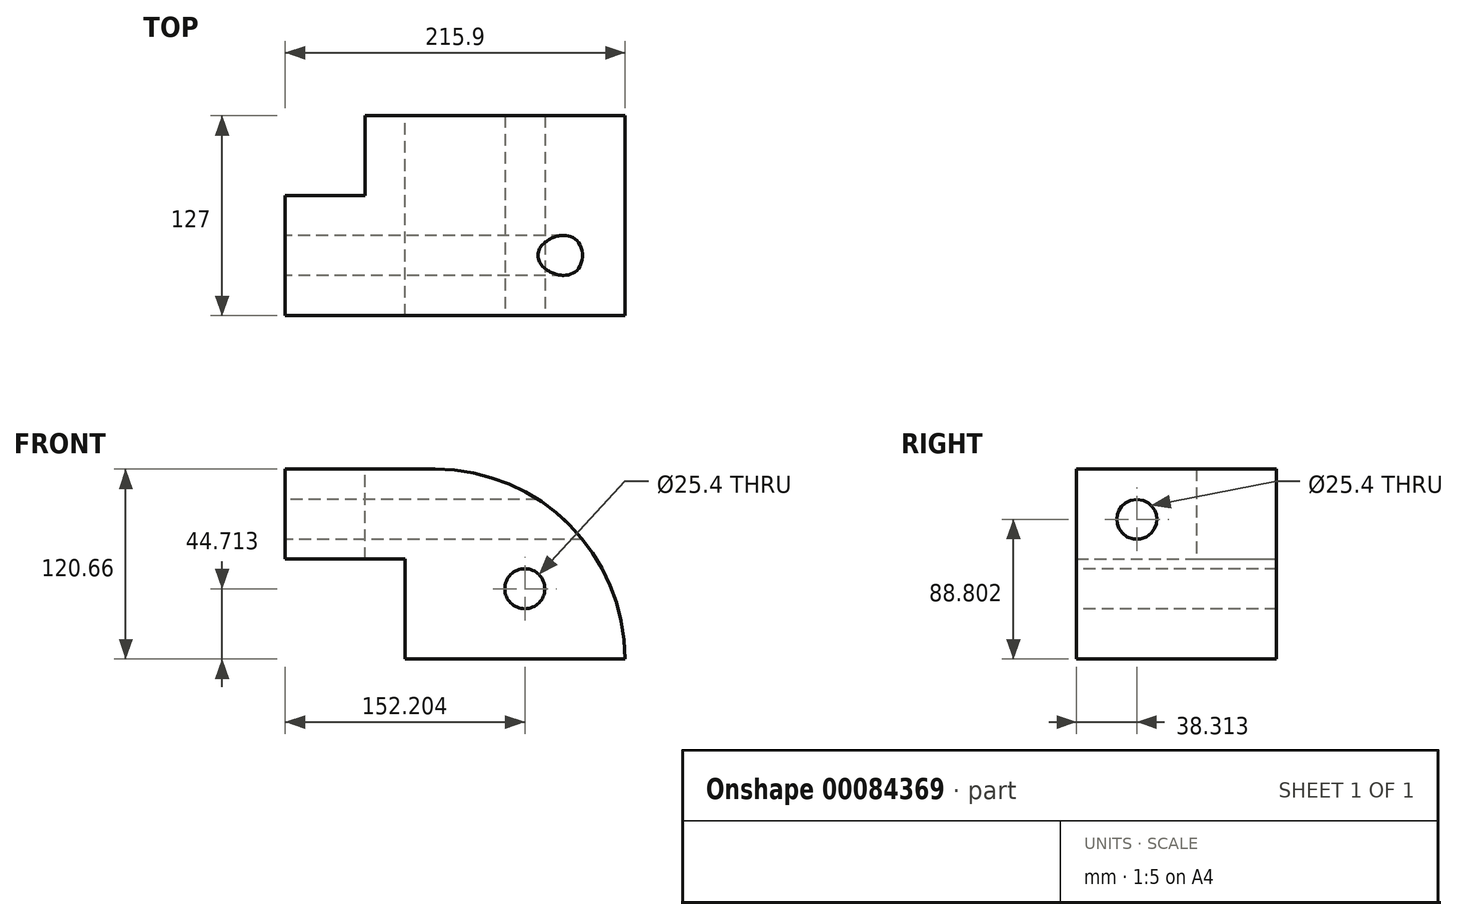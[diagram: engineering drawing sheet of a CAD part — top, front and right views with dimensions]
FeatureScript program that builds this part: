
annotation { "Feature Type Name" : "Feature", "Feature Type Description" : "" }
export const myFeature = defineFeature(function(context is Context, id is Id, definition is map)
    precondition{}
    {
        {
            var Q0;
            Q0=qCreatedBy(makeId("Right.planeOp"),FACE);
            var sketch = newSketch(context, id + "F0", { "sketchPlane" : qUnion([Q0])});
            skLineSegment(sketch, "E0.bottom", {"start": v(-63.5, -60.33) * mm, "end": v(63.5, -60.33) * mm});
            skLineSegment(sketch, "E0.top", {"start": v(-63.5, 60.33) * mm, "end": v(63.5, 60.33) * mm});
            skLineSegment(sketch, "E0.left", {"start": v(-63.5, -60.33) * mm, "end": v(-63.5, 60.33) * mm});
            skLineSegment(sketch, "E0.right", {"start": v(63.5, -60.33) * mm, "end": v(63.5, 60.33) * mm});
            skPoint(sketch, "E0.middle", {"position": v(0, 0) * mm});
            skSolve(sketch);
        }
        {
            var Q0;
            Q0=makeQuery(id+"F0.imprint","IMPRINT",FACE,{"disambiguationData":[TD([[makeQuery(id+"F0.imprint","IMPRINT",EDGE,{"derivedFrom":sQuery(id+"F0.wireOp",EDGE,"E0.bottom")}),1.0]])]});
            extrude(context, id + "F1", {"entities" : qUnion([Q0]), "depth" : 139.7 * mm});
        }
        {
            var Q0;
            Q0=makeQuery(id+"F1.opExtrude","CAP_FACE",FACE,{"disambiguationData":[OSD([sQuery(id+"F0.wireOp",EDGE,"E0.bottom"),sQuery(id+"F0.wireOp",EDGE,"E0.top"),sQuery(id+"F0.wireOp",EDGE,"E0.left"),sQuery(id+"F0.wireOp",EDGE,"E0.right")])],"isStart":true});
            var sketch = newSketch(context, id + "F2", { "sketchPlane" : qUnion([Q0])});
            skLineSegment(sketch, "E1.bottom", {"start": v(63.5, 60.33) * mm, "end": v(-12.7, 60.32) * mm});
            skLineSegment(sketch, "E1.top", {"start": v(63.5, 3.17) * mm, "end": v(-12.7, 3.17) * mm});
            skLineSegment(sketch, "E1.left", {"start": v(63.5, 60.33) * mm, "end": v(63.5, 3.17) * mm});
            skLineSegment(sketch, "E1.right", {"start": v(-12.7, 60.32) * mm, "end": v(-12.7, 3.17) * mm});
            skSolve(sketch);
        }
        {
            var Q0;
            Q0=makeQuery(id+"F2.imprint","IMPRINT",FACE,{"disambiguationData":[TD([[makeQuery(id+"F2.imprint","IMPRINT",EDGE,{"derivedFrom":sQuery(id+"F2.wireOp",EDGE,"E1.bottom")}),1.0]])]});
            extrude(context, id + "F3", {"entities" : qUnion([Q0]), "operationType" : NewBodyOperationType.ADD, "depth" : 76.2 * mm});
        }
        {
            var Q0;
            Q0=makeQuery(id+"F3.boolean.opBoolean","MERGE",FACE,{"derivedFrom":[makeQuery(id+"F1.opExtrude","SWEPT_FACE",FACE,{"disambiguationData":[OSD([sQuery(id+"F0.wireOp",EDGE,"E0.left")])]}),makeQuery(id+"F3.opExtrude","SWEPT_FACE",FACE,{"disambiguationData":[OSD([sQuery(id+"F2.wireOp",EDGE,"E1.left")])]})]});
            var sketch = newSketch(context, id + "F4", { "sketchPlane" : qUnion([Q0])});
            skArc(sketch, "E2", {"start": v(139.7, -60.32) * mm, "mid": v(104.36, 24.99) * mm, "end": v(19.05, 60.33) * mm});
            skSolve(sketch);
        }
        {
            var Q0;
            {var subQ0=sQuery(id+"F4.wireOp",EDGE,"E2");Q0=makeQuery(id+"F4.imprint","IMPRINT",FACE,{"disambiguationData":[TD([[makeQuery(id+"F4.imprint","IMPRINT",EDGE,{"derivedFrom":subQ0}),-1.0]])]});}
            extrude(context, id + "F5", {"entities" : qUnion([Q0]), "operationType" : NewBodyOperationType.REMOVE, "endBound" : BoundingType.THROUGH_ALL, "oppositeDirection" : true, "depth" : 25.4 * mm});
        }
        {
            var Q0;
            Q0=makeQuery(id+"F1.opExtrude","CAP_FACE",FACE,{"disambiguationData":[OSD([sQuery(id+"F0.wireOp",EDGE,"E0.bottom"),sQuery(id+"F0.wireOp",EDGE,"E0.top"),sQuery(id+"F0.wireOp",EDGE,"E0.left"),sQuery(id+"F0.wireOp",EDGE,"E0.right")])],"isStart":true});
            var sketch = newSketch(context, id + "F6", { "sketchPlane" : qUnion([Q0])});
            skLineSegment(sketch, "E3", {"start": v(-12.7, 3.17) * mm, "end": v(-63.5, 3.17) * mm});
            skSolve(sketch);
        }
        {
            var Q0;
            {var subQ0=sQuery(id+"F6.wireOp",EDGE,"E3");Q0=makeQuery(id+"F6.imprint","IMPRINT",FACE,{"disambiguationData":[TD([[makeQuery(id+"F6.imprint","IMPRINT",EDGE,{"derivedFrom":subQ0}),-1.0]])]});}
            extrude(context, id + "F7", {"entities" : qUnion([Q0]), "operationType" : NewBodyOperationType.ADD, "depth" : 25.4 * mm});
        }
        {
            var Q0;
            Q0=makeQuery(id+"F3.opExtrude","CAP_FACE",FACE,{"disambiguationData":[OSD([sQuery(id+"F2.wireOp",EDGE,"E1.bottom"),sQuery(id+"F2.wireOp",EDGE,"E1.top"),sQuery(id+"F2.wireOp",EDGE,"E1.left"),sQuery(id+"F2.wireOp",EDGE,"E1.right")])],"isStart":false});
            var sketch = newSketch(context, id + "F8", { "sketchPlane" : qUnion([Q0])});
            skLineSegment(sketch, "E4.bottom", {"start": v(63.5, 60.33) * mm, "end": v(25.4, 60.33) * mm});
            skLineSegment(sketch, "E4.top", {"start": v(63.5, 28.58) * mm, "end": v(25.4, 28.57) * mm});
            skLineSegment(sketch, "E4.left", {"start": v(63.5, 60.33) * mm, "end": v(63.5, 28.58) * mm});
            skLineSegment(sketch, "E4.right", {"start": v(25.4, 60.33) * mm, "end": v(25.4, 28.57) * mm});
            skSolve(sketch);
        }
        {
            var Q0;
            Q0=makeQuery(id+"F8.imprint","IMPRINT",FACE,{"disambiguationData":[TD([[makeQuery(id+"F8.imprint","IMPRINT",EDGE,{"derivedFrom":sQuery(id+"F8.wireOp",EDGE,"E4.bottom")}),1.0]])]});
            var sketch = newSketch(context, id + "F9", { "sketchPlane" : qUnion([Q0])});
            skCircle(sketch, "E5", {"center": v(25.19, 28.47) * mm, "radius": 12.7 * mm});
            skSolve(sketch);
        }
        {
            var Q0;
            Q0 = qSketchRegion(id + "F9", true);
            extrude(context, id + "F10", {"entities" : qUnion([Q0]), "operationType" : NewBodyOperationType.REMOVE, "endBound" : BoundingType.THROUGH_ALL, "oppositeDirection" : true, "depth" : 25.4 * mm});
        }
        {
            var Q0;
            Q0=makeQuery(id+"F3.boolean.opBoolean","MERGE",FACE,{"derivedFrom":[makeQuery(id+"F1.opExtrude","SWEPT_FACE",FACE,{"disambiguationData":[OSD([sQuery(id+"F0.wireOp",EDGE,"E0.left")])]}),makeQuery(id+"F3.opExtrude","SWEPT_FACE",FACE,{"disambiguationData":[OSD([sQuery(id+"F2.wireOp",EDGE,"E1.left")])]})]});
            var sketch = newSketch(context, id + "F11", { "sketchPlane" : qUnion([Q0])});
            skCircle(sketch, "E6", {"center": v(76, -15.62) * mm, "radius": 12.7 * mm});
            skSolve(sketch);
        }
        {
            var Q0;
            Q0 = qSketchRegion(id + "F11", true);
            extrude(context, id + "F12", {"entities" : qUnion([Q0]), "operationType" : NewBodyOperationType.REMOVE, "endBound" : BoundingType.THROUGH_ALL, "oppositeDirection" : true, "depth" : 25.4 * mm});
        }
    });
